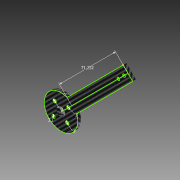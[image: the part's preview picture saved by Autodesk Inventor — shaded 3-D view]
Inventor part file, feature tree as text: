
AUTODESK INVENTOR PART (.ipt)
format: ipt  version: 2015 (Build 190159000, 159)  size: 101,376 bytes
history: native  units: mm
features: extrude x2, sketch x2
ambient origin geometry x8: Origin, YZ Plane, XZ Plane, XY Plane, X Axis, Y Axis, Z Axis, Center Point
bodies: Solid1 (feature_tree)
feature tree (4):
  extrude  "Extrusion1"  Depth=3.0mm
  extrude  "Extrusion2"  Depth=3.0mm
  sketch  "Sketch1"  dims[d3=3.0mm d4=3.0mm]
  sketch  "Sketch2"  dims[d5=3.0mm d6=3.0mm d7=3.0mm d8=0.0mm d9=8.0mm d10=3.0mm d11=0.0mm d12=71.252273mm]
